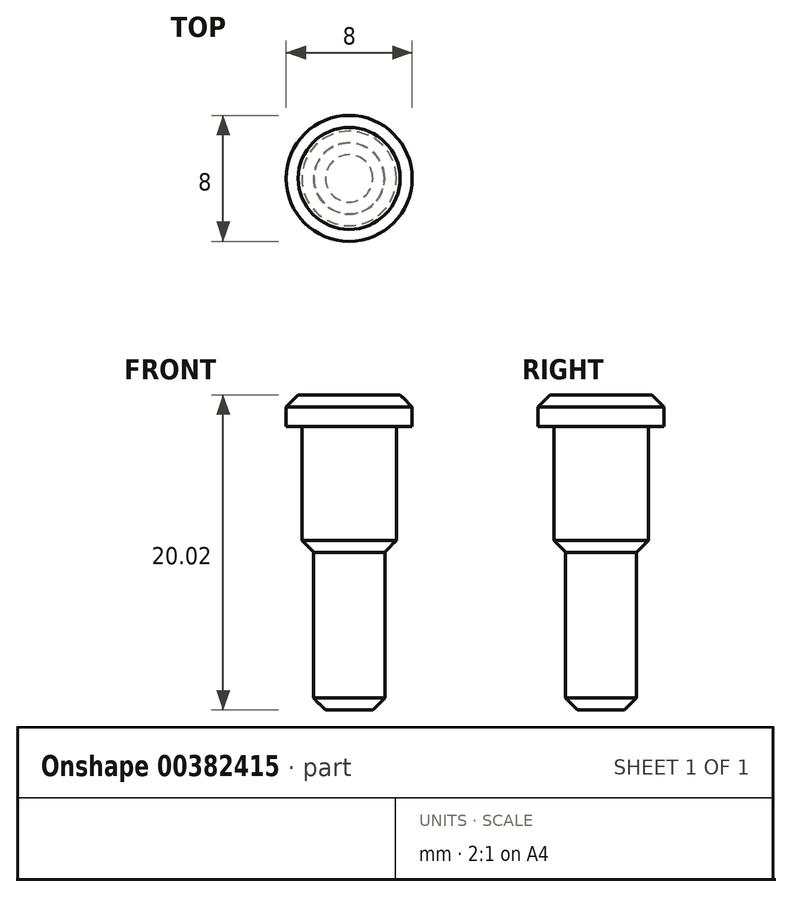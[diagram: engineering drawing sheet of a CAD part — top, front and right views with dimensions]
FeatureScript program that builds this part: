
annotation { "Feature Type Name" : "Feature", "Feature Type Description" : "" }
export const myFeature = defineFeature(function(context is Context, id is Id, definition is map)
    precondition{}
    {
        {
            var Q0;
            Q0=qCreatedBy(makeId("Top.planeOp"),FACE);
            var sketch = newSketch(context, id + "F0", { "sketchPlane" : qUnion([Q0])});
            skCircle(sketch, "E0", {"center": v(0, 0) * mm, "radius": 4 * mm});
            skCircle(sketch, "E1", {"center": v(0, 0) * mm, "radius": 3 * mm});
            skSolve(sketch);
        }
        {
            var Q0;
            Q0=makeQuery(id+"F0.imprint","IMPRINT",FACE,{"disambiguationData":[TD([[makeQuery(id+"F0.imprint","IMPRINT",EDGE,{"derivedFrom":sQuery(id+"F0.wireOp",EDGE,"E0")}),1.0]])]});
            var Q1;
            Q1=makeQuery(id+"F0.imprint","IMPRINT",FACE,{"disambiguationData":[TD([[makeQuery(id+"F0.imprint","IMPRINT",EDGE,{"derivedFrom":sQuery(id+"F0.wireOp",EDGE,"E1")}),1.0]])]});
            extrude(context, id + "F1", {"entities" : qUnion([Q0, Q1]), "depth" : 2 * mm});
        }
        {
            var Q0;
            Q0=makeQuery(id+"F1.opExtrude","CAP_FACE",FACE,{"disambiguationData":[OSD([sQuery(id+"F0.wireOp",EDGE,"E0")])],"isStart":false});
            chamfer(context, id + "F2", {"entities" : qUnion([Q0]), "width" : 0.76 * mm, "tangentPropagation" : true});
        }
        {
            var Q0;
            Q0=makeQuery(id+"F0.imprint","IMPRINT",FACE,{"disambiguationData":[TD([[makeQuery(id+"F0.imprint","IMPRINT",EDGE,{"derivedFrom":sQuery(id+"F0.wireOp",EDGE,"E1")}),1.0]])]});
            extrude(context, id + "F3", {"entities" : qUnion([Q0]), "operationType" : NewBodyOperationType.ADD, "oppositeDirection" : true, "depth" : 8 * mm});
        }
        {
            var Q0;
            Q0=makeQuery(id+"F3.opExtrude","CAP_FACE",FACE,{"disambiguationData":[OSD([sQuery(id+"F0.wireOp",EDGE,"E1")])],"isStart":false});
            var sketch = newSketch(context, id + "F4", { "sketchPlane" : qUnion([Q0])});
            skCircle(sketch, "E2", {"center": v(0, 0) * mm, "radius": 2.26 * mm});
            skSolve(sketch);
        }
        {
            var Q0;
            Q0=makeQuery(id+"F3.opExtrude","CAP_FACE",FACE,{"disambiguationData":[OSD([sQuery(id+"F0.wireOp",EDGE,"E1")])],"isStart":false});
            chamfer(context, id + "F5", {"entities" : qUnion([Q0]), "width" : 0.76 * mm, "tangentPropagation" : true});
        }
        {
            var Q0;
            Q0=makeQuery(id+"F4.imprint","IMPRINT",FACE,{"disambiguationData":[TD([[makeQuery(id+"F4.imprint","IMPRINT",EDGE,{"derivedFrom":sQuery(id+"F4.wireOp",EDGE,"E2")}),1.0]])]});
            extrude(context, id + "F6", {"entities" : qUnion([Q0]), "operationType" : NewBodyOperationType.ADD, "depth" : 10 * mm});
        }
        {
            var Q0;
            Q0=makeQuery(id+"F6.opExtrude","CAP_FACE",FACE,{"disambiguationData":[OSD([sQuery(id+"F4.wireOp",EDGE,"E2")])],"isStart":false});
            chamfer(context, id + "F7", {"entities" : qUnion([Q0]), "width" : 0.76 * mm, "tangentPropagation" : true});
        }
    });
